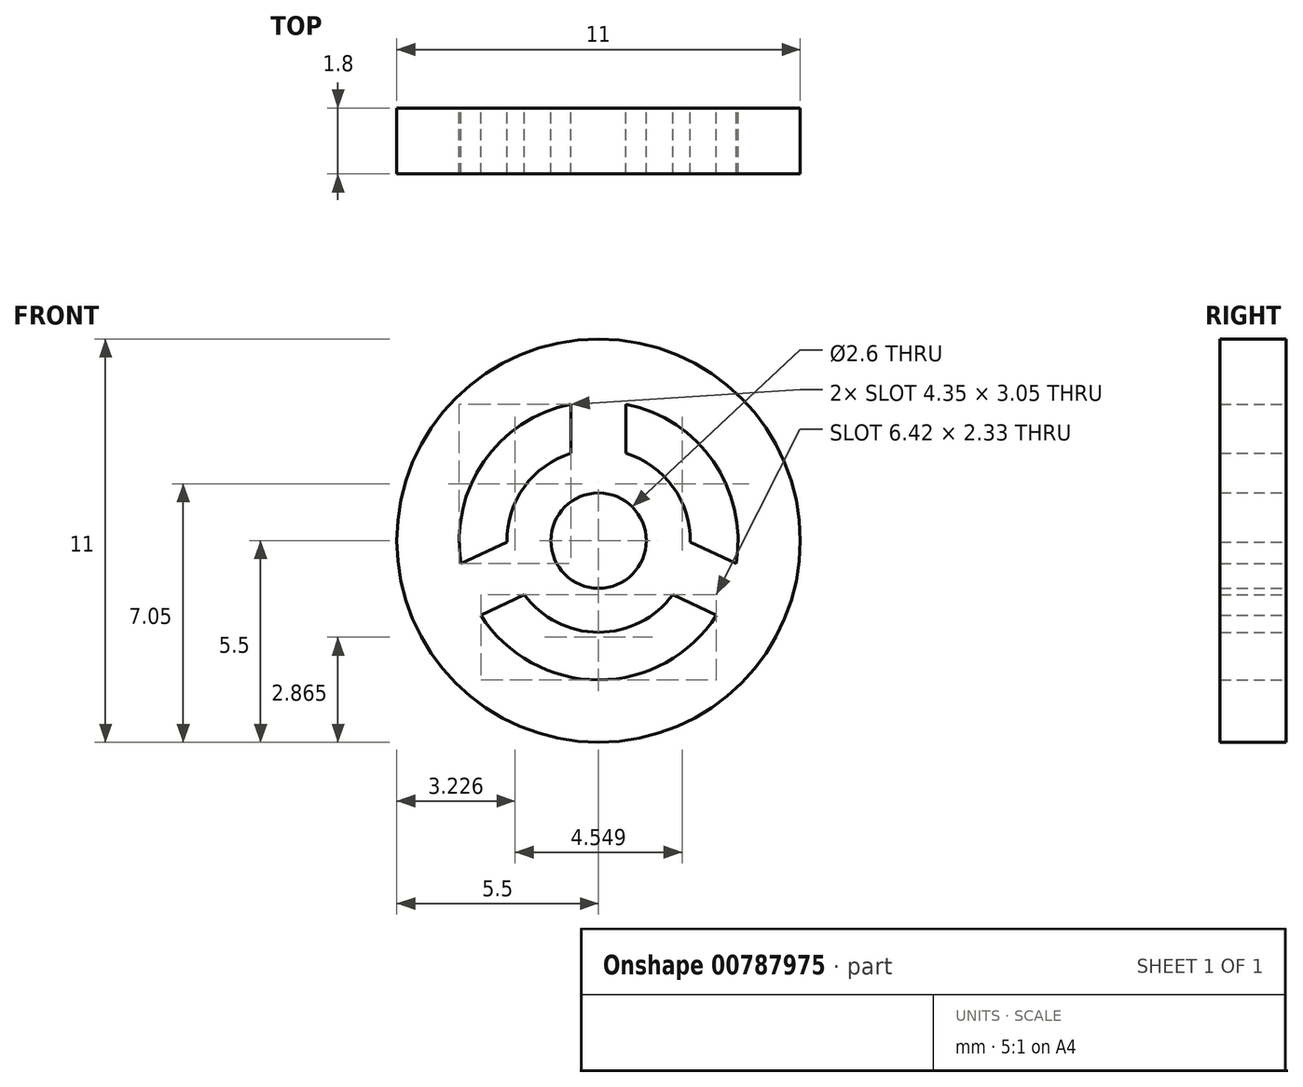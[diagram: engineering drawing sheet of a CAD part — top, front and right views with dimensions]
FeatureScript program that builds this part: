
annotation { "Feature Type Name" : "Feature", "Feature Type Description" : "" }
export const myFeature = defineFeature(function(context is Context, id is Id, definition is map)
    precondition{}
    {
        {
            var Q0;
            Q0=qCreatedBy(makeId("Front.planeOp"),FACE);
            var sketch = newSketch(context, id + "F0", { "sketchPlane" : qUnion([Q0])});
            skCircle(sketch, "E0", {"center": v(0, 0) * mm, "radius": 5.5 * mm});
            skCircle(sketch, "E1", {"center": v(0, 0) * mm, "radius": 2.5 * mm});
            skCircle(sketch, "E2", {"center": v(0, 0) * mm, "radius": 3.8 * mm});
            skLineSegment(sketch, "E3", {"start": v(-0.75, 2.38) * mm, "end": v(-0.75, 3.73) * mm});
            skLineSegment(sketch, "E4", {"start": v(0.75, 2.38) * mm, "end": v(0.75, 3.73) * mm});
            skLineSegment(sketch, "E5", {"start": v(-2.5, -0.04) * mm, "end": v(-3.75, -0.62) * mm});
            skLineSegment(sketch, "E6", {"start": v(-2.02, -1.47) * mm, "end": v(-3.21, -2.03) * mm});
            skLineSegment(sketch, "E7", {"start": v(2.5, -0.04) * mm, "end": v(3.75, -0.62) * mm});
            skLineSegment(sketch, "E8", {"start": v(2.02, -1.47) * mm, "end": v(3.21, -2.03) * mm});
            skCircle(sketch, "E9", {"center": v(0, 0) * mm, "radius": 1.3 * mm});
            skSolve(sketch);
        }
        {
            var Q0;
            Q0 = qSketchRegion(id + "F0", true);
            var Q1;
            {var subQ0=sQuery(id+"F0.wireOp",EDGE,"E7");Q1=makeQuery(id+"F0.imprint","IMPRINT",FACE,{"disambiguationData":[TD([[makeQuery(id+"F0.imprint","IMPRINT",EDGE,{"derivedFrom":subQ0}),-1.0]])]});}
            var Q2;
            {var subQ0=sQuery(id+"F0.wireOp",EDGE,"E3");Q2=makeQuery(id+"F0.imprint","IMPRINT",FACE,{"disambiguationData":[TD([[makeQuery(id+"F0.imprint","IMPRINT",EDGE,{"derivedFrom":subQ0}),-1.0]])]});}
            var Q3;
            {var subQ0=sQuery(id+"F0.wireOp",EDGE,"E5");Q3=makeQuery(id+"F0.imprint","IMPRINT",FACE,{"disambiguationData":[TD([[makeQuery(id+"F0.imprint","IMPRINT",EDGE,{"derivedFrom":subQ0}),1.0]])]});}
            var Q4;
            Q4=makeQuery(id+"F0.imprint","IMPRINT",FACE,{"disambiguationData":[TD([[makeQuery(id+"F0.imprint","IMPRINT",EDGE,{"derivedFrom":sQuery(id+"F0.wireOp",EDGE,"E9")}),-1.0]])]});
            extrude(context, id + "F1", {"entities" : qUnion([Q0, Q1, Q2, Q3, Q4]), "depth" : 1.8 * mm, "offsetDistance" : 25 * mm});
        }
    });
